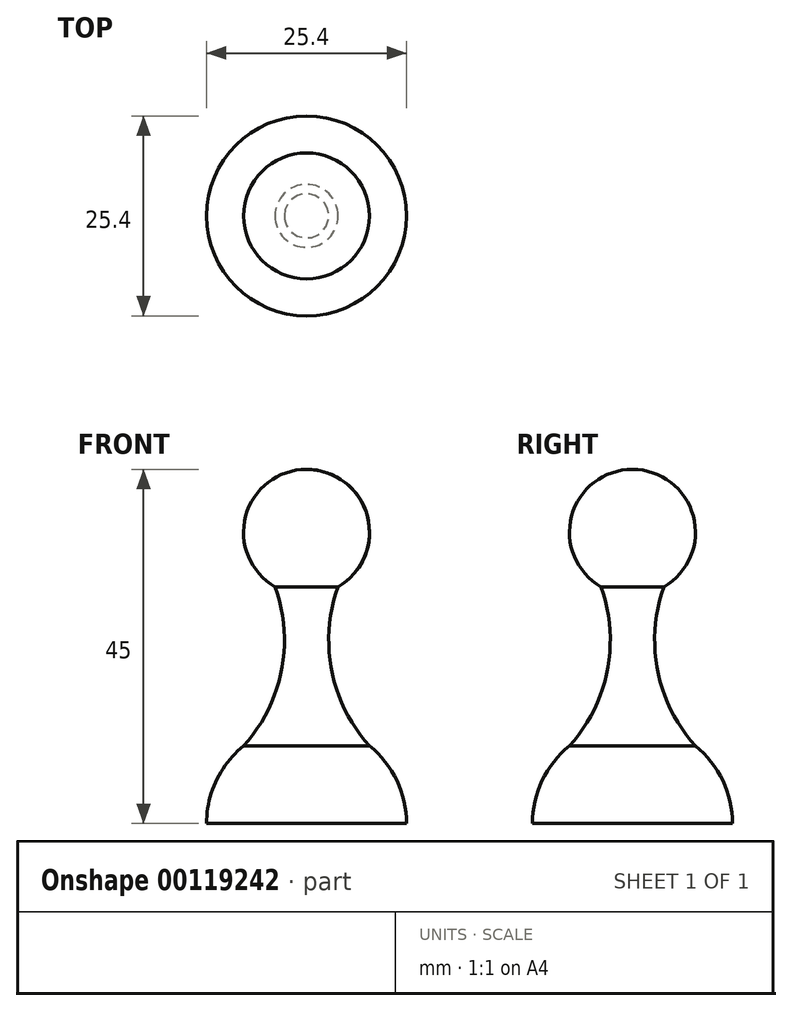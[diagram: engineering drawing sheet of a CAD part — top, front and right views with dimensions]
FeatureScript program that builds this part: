
annotation { "Feature Type Name" : "Feature", "Feature Type Description" : "" }
export const myFeature = defineFeature(function(context is Context, id is Id, definition is map)
    precondition{}
    {
        {
            var Q0;
            Q0=qCreatedBy(makeId("Front.planeOp"),FACE);
            var sketch = newSketch(context, id + "F0", { "sketchPlane" : qUnion([Q0])});
            skLineSegment(sketch, "E0", {"start": v(0, 0) * mm, "end": v(0, 45) * mm});
            skLineSegment(sketch, "E1", {"start": v(0, 0) * mm, "end": v(12.7, 0) * mm});
            skArc(sketch, "E2", {"start": v(12.7, 0) * mm, "mid": v(11.46, 5.46) * mm, "end": v(8, 9.86) * mm});
            skArc(sketch, "E3", {"start": v(0, 45) * mm, "mid": v(7.73, 39.07) * mm, "end": v(4, 30.07) * mm});
            skArc(sketch, "E4", {"start": v(8, 9.86) * mm, "mid": v(3.2, 19.41) * mm, "end": v(4, 30.07) * mm});
            skSolve(sketch);
        }
        {
            var Q0;
            Q0 = qSketchRegion(id + "F0", true);
            var Q1;
            Q1=sQuery(id+"F0.wireOp",EDGE,"E0");
            revolve(context, id + "F1", {"entities" : qUnion([Q0]), "axis" : qUnion([Q1]), "revolveType" : RevolveType.FULL});
        }
    });
